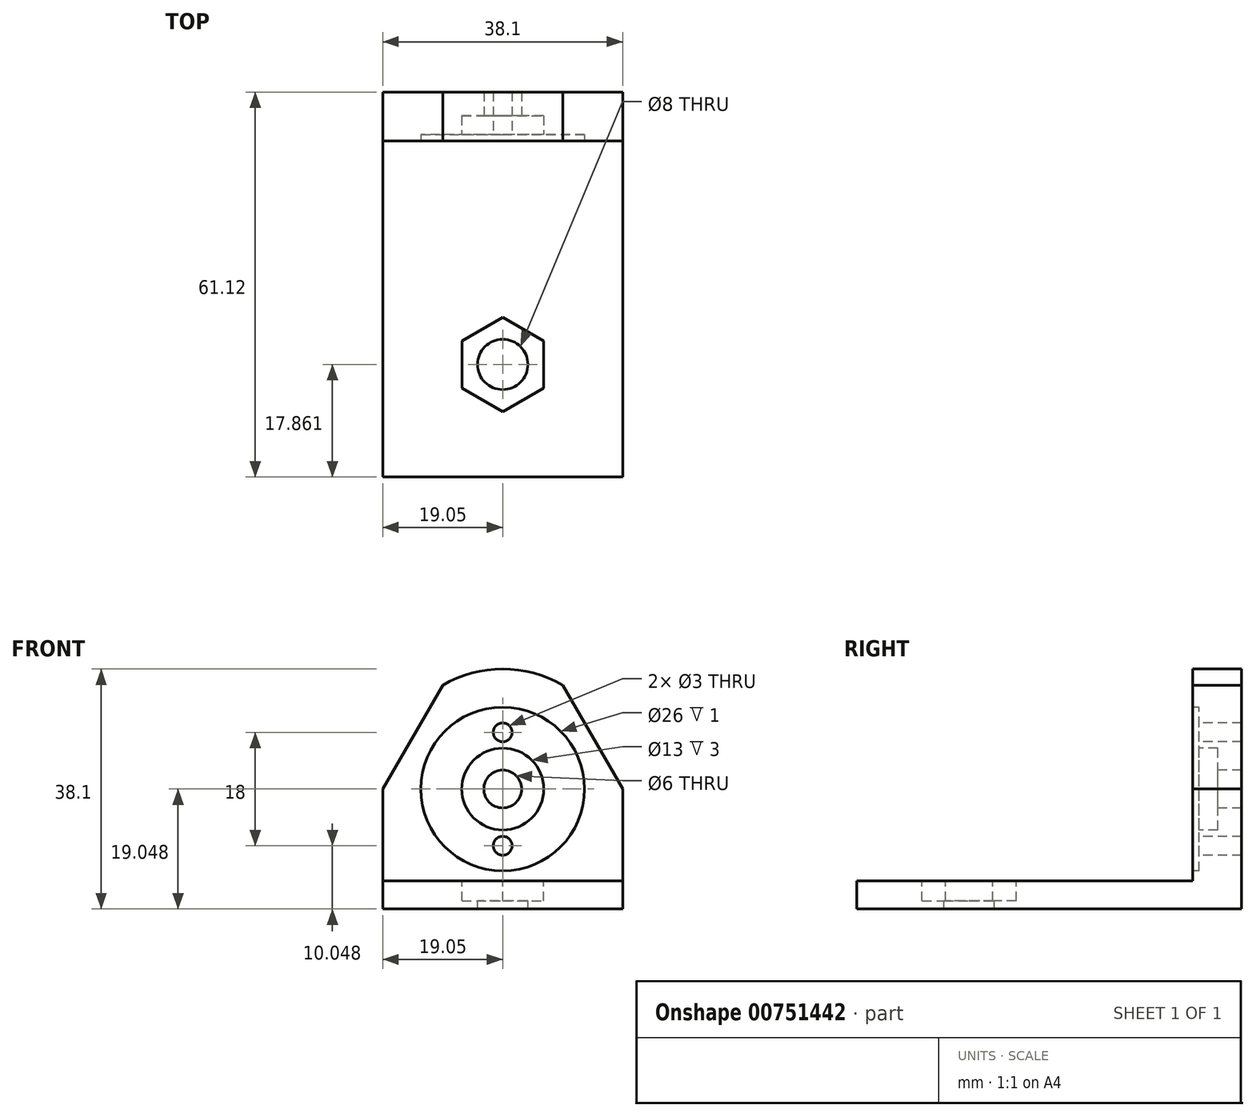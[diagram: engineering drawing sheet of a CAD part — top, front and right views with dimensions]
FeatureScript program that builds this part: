
annotation { "Feature Type Name" : "Feature", "Feature Type Description" : "" }
export const myFeature = defineFeature(function(context is Context, id is Id, definition is map)
    precondition{}
    {
        {
            var Q0;
            Q0=qCreatedBy(makeId("Front.planeOp"),FACE);
            var sketch = newSketch(context, id + "F0", { "sketchPlane" : qUnion([Q0])});
            skLineSegment(sketch, "E0.bottom", {"start": v(-38.1, 15.06) * mm, "end": v(38.1, 15.06) * mm, "construction": true});
            skLineSegment(sketch, "E0.top", {"start": v(-38.1, -15.06) * mm, "end": v(38.1, -15.06) * mm, "construction": true});
            skLineSegment(sketch, "E0.left", {"start": v(-38.1, 15.06) * mm, "end": v(-38.1, -15.06) * mm, "construction": true});
            skLineSegment(sketch, "E0.right", {"start": v(38.1, 15.06) * mm, "end": v(38.1, -15.06) * mm, "construction": true});
            skPoint(sketch, "E1", {"position": v(-38.1, 0) * mm});
            skPoint(sketch, "E2", {"position": v(0, 15.06) * mm});
            skCircle(sketch, "E3", {"center": v(-28.57, 1.45) * mm, "radius": 4.76 * mm, "construction": true});
            skArc(sketch, "E4", {"start": v(-11.11, 6.21) * mm, "mid": v(-15.88, 1.45) * mm, "end": v(-11.11, -3.31) * mm, "construction": true});
            skArc(sketch, "E5", {"start": v(-7.94, -3.31) * mm, "mid": v(-3.17, 1.45) * mm, "end": v(-7.94, 6.21) * mm, "construction": true});
            skLineSegment(sketch, "E6", {"start": v(-11.11, 6.21) * mm, "end": v(-7.94, 6.21) * mm, "construction": true});
            skLineSegment(sketch, "E7", {"start": v(-11.11, -3.31) * mm, "end": v(-7.94, -3.31) * mm, "construction": true});
            skArc(sketch, "E8", {"start": v(7.94, 6.21) * mm, "mid": v(3.18, 1.45) * mm, "end": v(7.94, -3.31) * mm, "construction": true});
            skArc(sketch, "E9", {"start": v(11.11, -3.31) * mm, "mid": v(15.88, 1.45) * mm, "end": v(11.11, 6.21) * mm, "construction": true});
            skLineSegment(sketch, "E10", {"start": v(7.94, 6.21) * mm, "end": v(11.11, 6.21) * mm, "construction": true});
            skLineSegment(sketch, "E11", {"start": v(7.94, -3.31) * mm, "end": v(11.11, -3.31) * mm, "construction": true});
            skCircle(sketch, "E12", {"center": v(28.57, 1.45) * mm, "radius": 4.76 * mm, "construction": true});
            skLineSegment(sketch, "E13.top", {"start": v(-38.1, -13.7) * mm, "end": v(38.1, -13.7) * mm, "construction": true});
            skLineSegment(sketch, "E13.left", {"start": v(-38.1, -15.06) * mm, "end": v(-38.1, -13.7) * mm, "construction": true});
            skLineSegment(sketch, "E13.right", {"start": v(38.1, -15.06) * mm, "end": v(38.1, -13.7) * mm, "construction": true});
            skCircle(sketch, "E14", {"center": v(0, 3.99) * mm, "radius": 6.35 * mm, "construction": true});
            skCircle(sketch, "E15", {"center": v(0, 3.99) * mm, "radius": 14.29 * mm, "construction": true});
            skCircle(sketch, "E16", {"center": v(0, 3.99) * mm, "radius": 50.8 * mm, "construction": true});
            skSolve(sketch);
        }
        {
            var Q0;
            Q0=qCreatedBy(makeId("Front.planeOp"),FACE);
            var sketch = newSketch(context, id + "F1", { "sketchPlane" : qUnion([Q0])});
            skArc(sketch, "E17", {"start": v(9.52, 20.49) * mm, "mid": v(0, 23.04) * mm, "end": v(-9.53, 20.49) * mm});
            skLineSegment(sketch, "E18.top", {"start": v(-19.05, -15.06) * mm, "end": v(19.05, -15.06) * mm});
            skLineSegment(sketch, "E18.left", {"start": v(-19.05, 3.99) * mm, "end": v(-19.05, -15.06) * mm});
            skLineSegment(sketch, "E18.right", {"start": v(19.05, 3.99) * mm, "end": v(19.05, -15.06) * mm});
            skLineSegment(sketch, "E19.bottom", {"start": v(-19.05, -10.62) * mm, "end": v(19.05, -10.62) * mm});
            skLineSegment(sketch, "E19.left", {"start": v(-19.05, -10.62) * mm, "end": v(-19.05, -15.06) * mm});
            skLineSegment(sketch, "E19.right", {"start": v(19.05, -10.62) * mm, "end": v(19.05, -15.06) * mm});
            skCircle(sketch, "E20", {"center": v(0, 3.99) * mm, "radius": 13 * mm});
            skCircle(sketch, "E21", {"center": v(0, 3.99) * mm, "radius": 9 * mm, "construction": true});
            skPoint(sketch, "E22", {"position": v(0, 12.99) * mm});
            skPoint(sketch, "E23", {"position": v(0, -5.01) * mm});
            skLineSegment(sketch, "E24", {"start": v(-19.05, 3.99) * mm, "end": v(-9.53, 20.49) * mm});
            skLineSegment(sketch, "E25", {"start": v(19.05, 3.99) * mm, "end": v(9.52, 20.49) * mm});
            skSolve(sketch);
        }
        {
            var Q0;
            Q0=makeQuery(id+"F1.imprint","IMPRINT",FACE,{"disambiguationData":[TD([[makeQuery(id+"F1.imprint","IMPRINT",EDGE,{"derivedFrom":sQuery(id+"F1.wireOp",EDGE,"E17")}),1.0]])]});
            var Q1;
            Q1=makeQuery(id+"F1.imprint","IMPRINT",FACE,{"disambiguationData":[TD([[makeQuery(id+"F1.imprint","IMPRINT",EDGE,{"derivedFrom":sQuery(id+"F1.wireOp",EDGE,"E18.top")}),1.0]])]});
            var Q2;
            Q2=makeQuery(id+"F1.imprint","IMPRINT",FACE,{"disambiguationData":[TD([[makeQuery(id+"F1.imprint","IMPRINT",EDGE,{"derivedFrom":sQuery(id+"F1.wireOp",EDGE,"E20")}),1.0]])]});
            extrude(context, id + "F2", {"entities" : qUnion([Q0, Q1, Q2]), "depth" : 3.8 * mm, "offsetDistance" : 25.4 * mm});
        }
        {
            var Q0;
            Q0=makeQuery(id+"F1.imprint","IMPRINT",FACE,{"disambiguationData":[TD([[makeQuery(id+"F1.imprint","IMPRINT",EDGE,{"derivedFrom":sQuery(id+"F1.wireOp",EDGE,"E18.top")}),1.0]])]});
            extrude(context, id + "F3", {"entities" : qUnion([Q0]), "operationType" : NewBodyOperationType.ADD, "depth" : 57.15 * mm, "offsetDistance" : 25.4 * mm});
        }
        {
            var Q0;
            Q0=makeQuery(id+"F3.opExtrude","SWEPT_FACE",FACE,{"disambiguationData":[OSD([sQuery(id+"F1.wireOp",EDGE,"E19.bottom")])]});
            var sketch = newSketch(context, id + "F4", { "sketchPlane" : qUnion([Q0])});
            skLineSegment(sketch, "E26", {"start": v(0, -3.81) * mm, "end": v(0, -57.15) * mm, "construction": true});
            skPoint(sketch, "E26.startSnap0", {"position": v(0, -3.81) * mm});
            skCircle(sketch, "E27", {"center": v(0, -39.29) * mm, "radius": 4 * mm});
            skCircle(sketch, "E28.cCircle", {"center": v(0, -39.29) * mm, "radius": 6.48 * mm, "construction": true});
            skLineSegment(sketch, "E28.0", {"start": v(6.48, -35.55) * mm, "end": v(6.48, -43.03) * mm});
            skLineSegment(sketch, "E28.1", {"start": v(6.48, -43.03) * mm, "end": v(0, -46.77) * mm});
            skLineSegment(sketch, "E28.2", {"start": v(0, -46.77) * mm, "end": v(-6.48, -43.03) * mm});
            skLineSegment(sketch, "E28.3", {"start": v(-6.48, -43.03) * mm, "end": v(-6.48, -35.55) * mm});
            skLineSegment(sketch, "E28.4", {"start": v(-6.48, -35.55) * mm, "end": v(0, -31.81) * mm});
            skLineSegment(sketch, "E28.5", {"start": v(0, -31.81) * mm, "end": v(6.48, -35.55) * mm});
            skPoint(sketch, "E28.0.midPoint", {"position": v(6.48, -39.29) * mm});
            skSolve(sketch);
        }
        {
            var Q0;
            Q0=makeQuery(id+"F4.imprint","IMPRINT",FACE,{"disambiguationData":[TD([[makeQuery(id+"F4.imprint","IMPRINT",EDGE,{"derivedFrom":sQuery(id+"F4.wireOp",EDGE,"E27")}),-1.0]])]});
            extrude(context, id + "F5", {"entities" : qUnion([Q0]), "operationType" : NewBodyOperationType.REMOVE, "oppositeDirection" : true, "depth" : 3.17 * mm, "offsetDistance" : 25.4 * mm});
        }
        {
            var Q0;
            Q0=makeQuery(id+"F4.imprint","IMPRINT",FACE,{"disambiguationData":[TD([[makeQuery(id+"F4.imprint","IMPRINT",EDGE,{"derivedFrom":sQuery(id+"F4.wireOp",EDGE,"E27")}),1.0]])]});
            extrude(context, id + "F6", {"entities" : qUnion([Q0]), "operationType" : NewBodyOperationType.REMOVE, "endBound" : BoundingType.THROUGH_ALL, "oppositeDirection" : true, "depth" : 25.4 * mm, "offsetDistance" : 25.4 * mm});
        }
        {
            var Q0;
            {var subQ0=sQuery(id+"F1.wireOp",EDGE,"iQXNbT1D-clqU-qqRB-6sf5-SRBJQL1cwo9m");Q0=makeQuery(id+"FKX1ockFk3IyBFj_1.boolean.opBoolean","MERGE",FACE,{"derivedFrom":[makeQuery(id+"F2.opExtrude","CAP_FACE",FACE,{"disambiguationData":[OSD([sQuery(id+"F1.wireOp",EDGE,"E17"),subQ0,sQuery(id+"F1.wireOp",EDGE,"E18.left"),sQuery(id+"F1.wireOp",EDGE,"E18.right"),sQuery(id+"F1.wireOp",EDGE,"E18.top"),sQuery(id+"F1.wireOp",EDGE,"E19.left"),sQuery(id+"F1.wireOp",EDGE,"E19.right")])],"isStart":true}),makeQuery(id+"FKX1ockFk3IyBFj_1.opExtrude","CAP_FACE",FACE,{"disambiguationData":[OSD([subQ0,sQuery(id+"F1.wireOp",EDGE,"aXmpQwUO-u038-tMxC-P9TH-Vx3ILCbJ5FUc")])],"isStart":true})]});}
            extrude(context, id + "F7", {"entities" : qUnion([Q0]), "operationType" : NewBodyOperationType.ADD, "depth" : 3.97 * mm, "offsetDistance" : 25.4 * mm});
        }
        {
            var Q0;
            Q0=makeQuery(id+"F2.opExtrude","CAP_FACE",FACE,{"disambiguationData":[OSD([sQuery(id+"F1.wireOp",EDGE,"E17"),sQuery(id+"F1.wireOp",EDGE,"E18.left"),sQuery(id+"F1.wireOp",EDGE,"E18.right"),sQuery(id+"F1.wireOp",EDGE,"E18.top"),sQuery(id+"F1.wireOp",EDGE,"E19.left"),sQuery(id+"F1.wireOp",EDGE,"E19.right")])],"isStart":false});
            var sketch = newSketch(context, id + "F8", { "sketchPlane" : qUnion([Q0])});
            skCircle(sketch, "E29", {"center": v(0, 3.99) * mm, "radius": 13 * mm});
            skCircle(sketch, "E30", {"center": v(0, 3.99) * mm, "radius": 6.5 * mm});
            skCircle(sketch, "E31", {"center": v(0, 3.99) * mm, "radius": 3 * mm});
            skPoint(sketch, "E32", {"position": v(0, 12.99) * mm});
            skPoint(sketch, "E33", {"position": v(0, -5.01) * mm});
            skSolve(sketch);
        }
        {
            var Q0;
            Q0=makeQuery(id+"F8.imprint","IMPRINT",FACE,{"disambiguationData":[TD([[makeQuery(id+"F8.imprint","IMPRINT",EDGE,{"derivedFrom":sQuery(id+"F8.wireOp",EDGE,"E29")}),1.0]])]});
            extrude(context, id + "F9", {"entities" : qUnion([Q0]), "operationType" : NewBodyOperationType.REMOVE, "oppositeDirection" : true, "depth" : 1 * mm, "offsetDistance" : 25.4 * mm});
        }
        {
            var Q0;
            Q0=makeQuery(id+"F9.boolean.opBoolean","SPLIT",FACE,{"disambiguationData":[TD([makeQuery(id+"F9.opExtrude","SWEPT_FACE",FACE,{"disambiguationData":[OSD([sQuery(id+"F8.wireOp",EDGE,"E30")])]})])],"derivedFrom":makeQuery(id+"F2.opExtrude","CAP_FACE",FACE,{"disambiguationData":[OSD([sQuery(id+"F1.wireOp",EDGE,"E17"),sQuery(id+"F1.wireOp",EDGE,"E18.left"),sQuery(id+"F1.wireOp",EDGE,"E18.right"),sQuery(id+"F1.wireOp",EDGE,"E18.top"),sQuery(id+"F1.wireOp",EDGE,"E19.left"),sQuery(id+"F1.wireOp",EDGE,"E19.right")])],"isStart":false})});
            extrude(context, id + "F10", {"entities" : qUnion([Q0]), "operationType" : NewBodyOperationType.REMOVE, "oppositeDirection" : true, "depth" : 4 * mm, "offsetDistance" : 25.4 * mm});
        }
        {
            var Q0;
            Q0=makeQuery(id+"F8.imprint","IMPRINT",FACE,{"disambiguationData":[TD([[makeQuery(id+"F8.imprint","IMPRINT",EDGE,{"derivedFrom":sQuery(id+"F8.wireOp",EDGE,"E31")}),1.0]])]});
            extrude(context, id + "F11", {"entities" : qUnion([Q0]), "operationType" : NewBodyOperationType.REMOVE, "endBound" : BoundingType.THROUGH_ALL, "oppositeDirection" : true, "depth" : 25.4 * mm, "offsetDistance" : 25.4 * mm});
        }
        {
            var Q0;
            Q0=sQuery(id+"F8.wireOp",VERTEX,"E32");
            var Q1;
            Q1=sQuery(id+"F8.wireOp",VERTEX,"E33");
            var Q2;
            Q2=makeQuery(id+"F2.opExtrude","SWEPT_BODY",BODY,{"disambiguationData":[OSD([sQuery(id+"F1.wireOp",EDGE,"E17"),sQuery(id+"F1.wireOp",EDGE,"E18.left"),sQuery(id+"F1.wireOp",EDGE,"E18.right"),sQuery(id+"F1.wireOp",EDGE,"E18.top"),sQuery(id+"F1.wireOp",EDGE,"E19.left"),sQuery(id+"F1.wireOp",EDGE,"E19.right")])]});
            hole(context, id + "F12", {"style" : HoleStyle.SIMPLE, "endStyle" : HoleEndStyle.THROUGH, "standardTappedOrClearance" : lookupTablePath({ "standard" : "ISO", "size" : "3", "type" : "Drilled" }), "standardBlindInLast" : lookupTablePath({ "standard" : "ISO", "size" : "3", "type" : "Drilled" }), "holeDiameter" : 3 * mm, "majorDiameter" : 6.35 * mm, "isTappedThrough" : true, "tappedDepth" : 12.7 * mm, "tapClearance" : 3, "locations" : qUnion([Q0, Q1]), "scope" : qUnion([Q2])});
        }
    });
